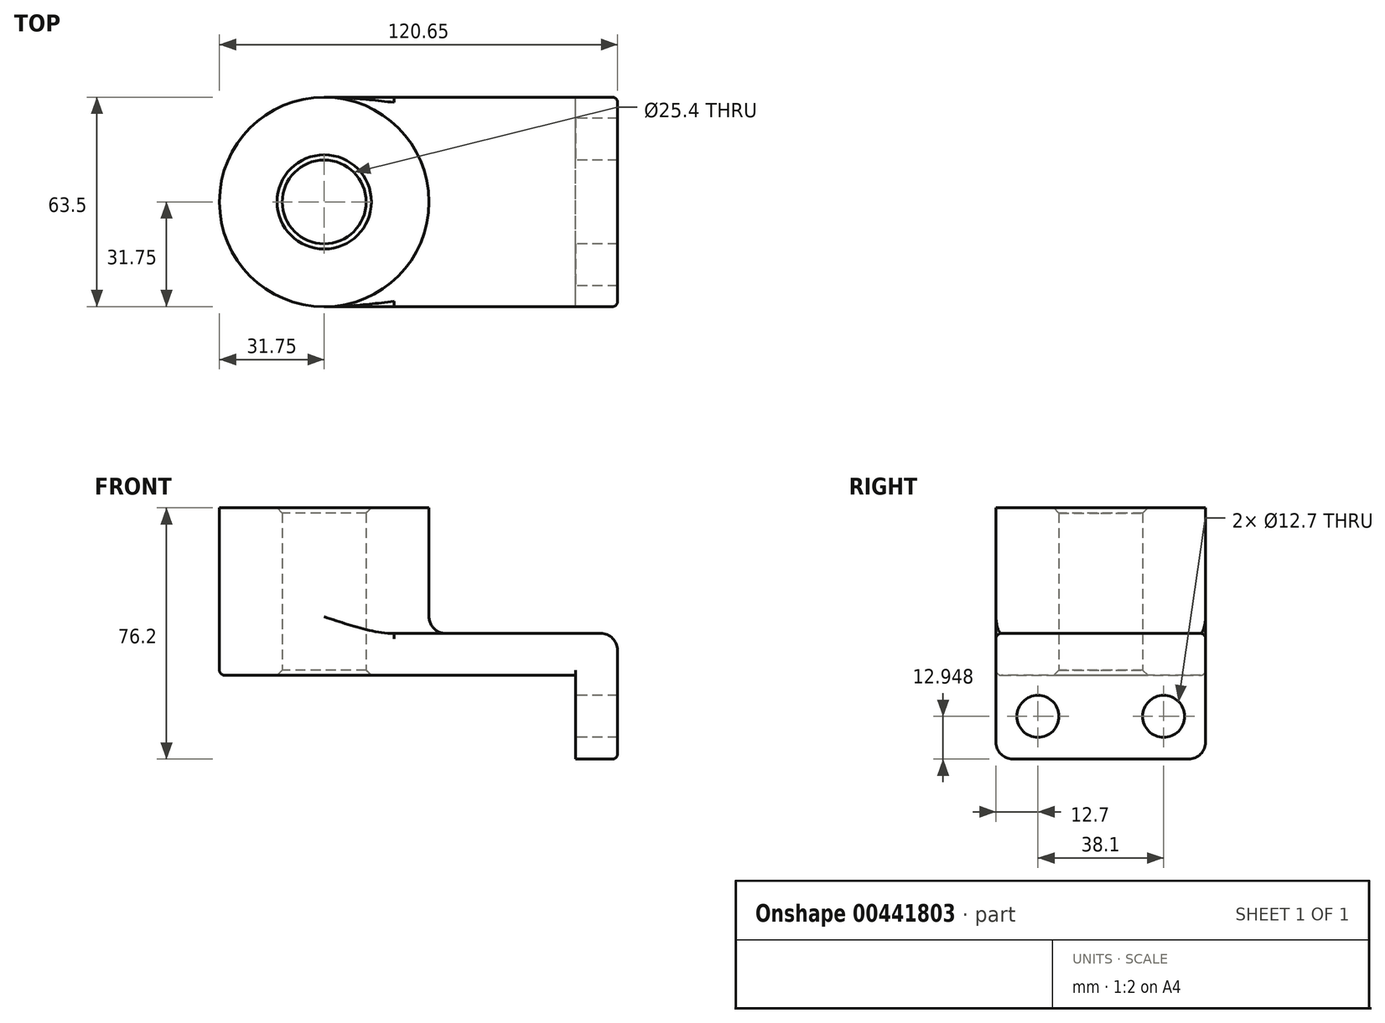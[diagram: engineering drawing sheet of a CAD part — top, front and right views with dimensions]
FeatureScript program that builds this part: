
annotation { "Feature Type Name" : "Feature", "Feature Type Description" : "" }
export const myFeature = defineFeature(function(context is Context, id is Id, definition is map)
    precondition{}
    {
        {
            var Q0;
            Q0=qCreatedBy(makeId("Top.planeOp"),FACE);
            var sketch = newSketch(context, id + "F0", { "sketchPlane" : qUnion([Q0])});
            skLineSegment(sketch, "E0.rect.bottom", {"start": v(-38.1, -31.75) * mm, "end": v(38.1, -31.75) * mm});
            skLineSegment(sketch, "E0.rect.top", {"start": v(-38.1, 31.75) * mm, "end": v(38.1, 31.75) * mm});
            skLineSegment(sketch, "E0.rect.left", {"start": v(-38.1, -31.75) * mm, "end": v(-38.1, 31.75) * mm});
            skLineSegment(sketch, "E0.rect.right", {"start": v(38.1, -31.75) * mm, "end": v(38.1, 31.75) * mm});
            skPoint(sketch, "E0.rect.middle", {"position": v(0, 0) * mm});
            skCircle(sketch, "E1", {"center": v(-38.1, 0) * mm, "radius": 31.75 * mm});
            skCircle(sketch, "E2", {"center": v(-38.1, 0) * mm, "radius": 12.7 * mm});
            skSolve(sketch);
        }
        {
            var Q0;
            Q0=qSketchRegion(id+"F0",true);
            extrude(context, id + "F1", {"entities" : qUnion([Q0]), "depth" : 12.7 * mm});
        }
        {
            var Q0;
            {var subQ0=sQuery(id+"F0.wireOp",EDGE,"E2");var subQ1=sQuery(id+"F0.wireOp",EDGE,"E0.rect.left");var subQ3=makeQuery(id+"F0.imprint","INTERSECT",VERTEX,{"disambiguationData":[OD(0.0)],"derivedFrom":[subQ1,subQ0]});Q0=makeQuery(id+"F0.imprint","IMPRINT",FACE,{"disambiguationData":[TD([[makeQuery(id+"F0.imprint","IMPRINT",EDGE,{"disambiguationData":[TD([[subQ3,1.0]])],"derivedFrom":subQ0}),-1.0]])]});}
            var Q1;
            {var subQ0=sQuery(id+"F0.wireOp",EDGE,"E2");var subQ1=sQuery(id+"F0.wireOp",EDGE,"E0.rect.left");var subQ3=makeQuery(id+"F0.imprint","INTERSECT",VERTEX,{"disambiguationData":[OD(0.0)],"derivedFrom":[subQ1,subQ0]});Q1=makeQuery(id+"F0.imprint","IMPRINT",FACE,{"disambiguationData":[TD([[makeQuery(id+"F0.imprint","IMPRINT",EDGE,{"disambiguationData":[TD([[subQ3,-1.0]])],"derivedFrom":subQ0}),-1.0]])]});}
            extrude(context, id + "F2", {"entities" : qUnion([Q0, Q1]), "operationType" : NewBodyOperationType.ADD, "depth" : 50.8 * mm});
        }
        {
            var Q0;
            Q0=makeQuery(id+"F1.opExtrude","SWEPT_FACE",FACE,{"disambiguationData":[OSD([sQuery(id+"F0.wireOp",EDGE,"E0.rect.right")])]});
            var sketch = newSketch(context, id + "F3", { "sketchPlane" : qUnion([Q0])});
            skLineSegment(sketch, "E3.bottom", {"start": v(-31.75, 12.7) * mm, "end": v(31.75, 12.7) * mm});
            skLineSegment(sketch, "E3.top", {"start": v(-31.75, -25.4) * mm, "end": v(31.75, -25.4) * mm});
            skLineSegment(sketch, "E3.left", {"start": v(-31.75, 12.7) * mm, "end": v(-31.75, -25.4) * mm});
            skLineSegment(sketch, "E3.right", {"start": v(31.75, 12.7) * mm, "end": v(31.75, -25.4) * mm});
            skCircle(sketch, "E4", {"center": v(-19.05, -12.45) * mm, "radius": 6.35 * mm});
            skLineSegment(sketch, "E5", {"start": v(0, 0) * mm, "end": v(0, -25.4) * mm});
            skCircle(sketch, "E6.MirrorC", {"center": v(19.05, -12.45) * mm, "radius": 6.35 * mm});
            skSolve(sketch);
        }
        {
            var Q0;
            Q0=qSketchRegion(id+"F3",true);
            extrude(context, id + "F4", {"entities" : qUnion([Q0]), "operationType" : NewBodyOperationType.ADD, "depth" : 12.7 * mm});
        }
        {
            var Q0;
            {var subQ0=sQuery(id+"F0.wireOp",EDGE,"E1");Q0=makeQuery(id+"F2.boolean.opBoolean","INTERSECT",EDGE,{"derivedFrom":[makeQuery(id+"F1.opExtrude","CAP_FACE",FACE,{"disambiguationData":[OSD([sQuery(id+"F0.wireOp",EDGE,"E0.rect.bottom"),sQuery(id+"F0.wireOp",EDGE,"E0.rect.top"),sQuery(id+"F0.wireOp",EDGE,"E0.rect.right"),subQ0,sQuery(id+"F0.wireOp",EDGE,"E2")])],"isStart":false}),makeQuery(id+"F2.opExtrude","SWEPT_FACE",FACE,{"disambiguationData":[OSD([subQ0])]})]});}
            var Q1;
            Q1=makeQuery(id+"F4.opExtrude","SWEPT_EDGE",EDGE,{"disambiguationData":[OSD([sQuery(id+"F3.wireOp",EDGE,"E3.top"),sQuery(id+"F3.wireOp",EDGE,"E3.left")])]});
            var Q2;
            Q2=makeQuery(id+"F4.opExtrude","SWEPT_EDGE",EDGE,{"disambiguationData":[OSD([sQuery(id+"F3.wireOp",EDGE,"E3.top"),sQuery(id+"F3.wireOp",EDGE,"E3.right")])]});
            var Q3;
            Q3=makeQuery(id+"F4.opExtrude","CAP_EDGE",EDGE,{"disambiguationData":[OSD([sQuery(id+"F3.wireOp",EDGE,"E3.bottom")])],"isStart":false});
            fillet(context, id + "F5", {"entities" : qUnion([Q0, Q1, Q2, Q3]), "radius" : 5.08 * mm, "tangentPropagation" : true, "allowEdgeOverflow" : false});
        }
        {
            var Q0;
            Q0=makeQuery(id+"F4.boolean.opBoolean","MERGE",EDGE,{"derivedFrom":[makeQuery(id+"F1.opExtrude","CAP_EDGE",EDGE,{"disambiguationData":[OSD([sQuery(id+"F0.wireOp",EDGE,"E0.rect.bottom")])],"isStart":false}),makeQuery(id+"F4.opExtrude","SWEPT_EDGE",EDGE,{"disambiguationData":[OSD([sQuery(id+"F3.wireOp",EDGE,"E3.bottom"),sQuery(id+"F3.wireOp",EDGE,"E3.left")])]})]});
            var Q1;
            Q1=makeQuery(id+"F1.opExtrude","CAP_EDGE",EDGE,{"disambiguationData":[OSD([sQuery(id+"F0.wireOp",EDGE,"E0.rect.bottom")])],"isStart":true});
            var Q2;
            Q2=makeQuery(id+"F1.opExtrude","CAP_EDGE",EDGE,{"disambiguationData":[OSD([sQuery(id+"F0.wireOp",EDGE,"E0.rect.right")])],"isStart":true});
            fillet(context, id + "F6", {"entities" : qUnion([Q0, Q1, Q2]), "radius" : 1.59 * mm, "tangentPropagation" : true, "allowEdgeOverflow" : false});
        }
        {
            var Q0;
            {var subQ0=sQuery(id+"F0.wireOp",EDGE,"E2");Q0=makeQuery(id+"F2.boolean.opBoolean","MERGE",FACE,{"derivedFrom":[makeQuery(id+"F1.opExtrude","SWEPT_FACE",FACE,{"disambiguationData":[OSD([subQ0])]}),makeQuery(id+"F2.opExtrude","SWEPT_FACE",FACE,{"disambiguationData":[OSD([subQ0])]})]});}
            chamfer(context, id + "F7", {"entities" : qUnion([Q0]), "width" : 1.59 * mm, "tangentPropagation" : true});
        }
    });
